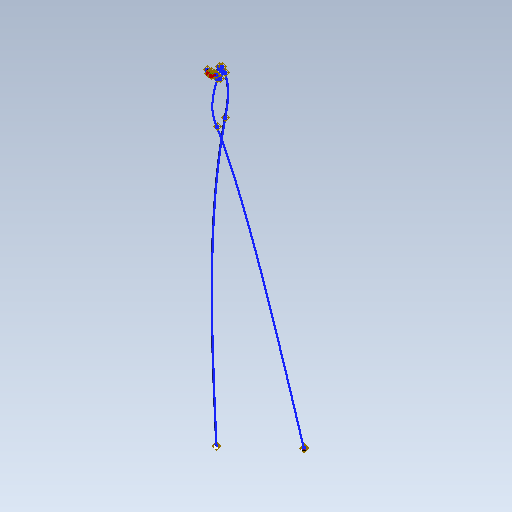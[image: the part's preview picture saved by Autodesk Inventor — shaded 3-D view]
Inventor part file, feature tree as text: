
AUTODESK INVENTOR PART (.ipt)
format: ipt  version: 2020 (Build 240168000, 168)  size: 187,904 bytes
history: native  units: mm (DEFAULTED — no unit token found)
features: other x49, plane x2, sketch x2
bodies: Body1 (feature_tree)
feature tree (53):
  other  "Origen"
  other  "Punto de trabajo1"
  other  "Punto de trabajo2"
  other  "Segmento1"
  other  "Punto de trabajo3"
  other  "Punto de trabajo4"
  other  "Punto de trabajo5"
  other  "Punto de trabajo6"
  plane  "Plano de trabajo1"
  other  "Punto de trabajo7"
  other  "Punto de trabajo8"
  other  "Segmento2"
  other  "Punto de trabajo9"
  other  "Punto de trabajo10"
  other  "Punto de trabajo11"
  other  "Punto de trabajo12"
  plane  "Plano de trabajo2"
  other  "Punto de trabajo13"
  other  "Punto de trabajo14"
  other  "Cable1:1"
  other  "Punto de trabajo15"
  other  "Punto de trabajo16"
  other  "Cable1:2"
  other  "Punto de trabajo17"
  other  "Punto de trabajo18"
  other  "Cable1:3"
  other  "Punto de trabajo19"
  other  "Punto de trabajo20"
  other  "Cable1:4"
  other  "Punto de trabajo21"
  other  "Punto de trabajo22"
  other  "Cable2:1"
  other  "Punto de trabajo23"
  other  "Punto de trabajo24"
  other  "Cable2:2"
  other  "Punto de trabajo25"
  other  "Punto de trabajo26"
  other  "Cable2:3"
  other  "Punto de trabajo27"
  other  "Punto de trabajo28"
  other  "Cable2:4"
  other  "Plano YZ"
  other  "Plano XZ"
  other  "Plano XY"
  other  "Eje X"
  other  "Eje Y"
  other  "Eje Z"
  sketch  "Boceto1"  dims[d0=0.0mm d1=0.0mm]
  other  "Sup1"
  sketch  "Boceto2"  dims[d2=0.0mm d3=0.0mm]
  other  "Sup2"
  other  "SuperficieBarrido1"
  other  "SuperficieBarrido2"
